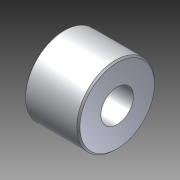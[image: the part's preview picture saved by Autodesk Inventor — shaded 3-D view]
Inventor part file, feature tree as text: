
AUTODESK INVENTOR PART (.ipt)
format: ipt  version: 2014 SP1 (Build 180222100, 222)  size: 94,208 bytes
history: native  units: in
note: dims shown in document units (in); Inventor stores cm internally (conversion verified against a paired STEP export)
features: chamfer x1, other x1, imported_body x1
ambient origin geometry x8: Origin, YZ Plane, XZ Plane, XY Plane, X Axis, Y Axis, Z Axis, Center Point
bodies: Body1 (feature_tree)
feature tree (3):
  chamfer  "Chamfer1"  [1 undecoded]
  other  "8mm spacer.ipt1"
  imported_body  "Base1"
note: 1 required parameter value undecoded (feature->parameter linkage not recoverable at this tier; creation-order binding heuristic only, values carry confidence <= 0.55)
